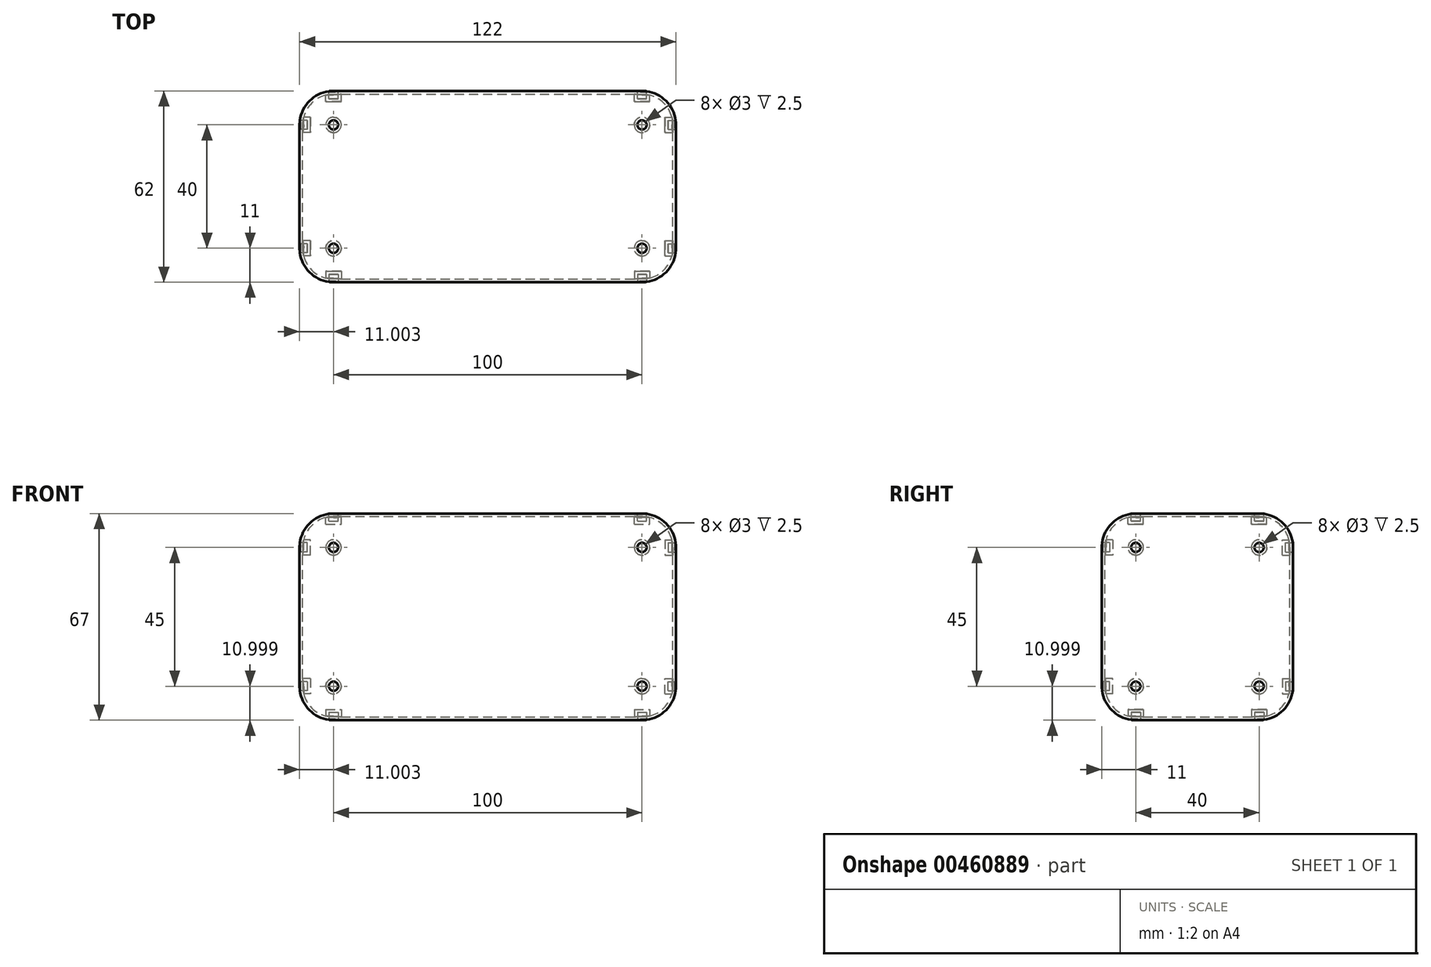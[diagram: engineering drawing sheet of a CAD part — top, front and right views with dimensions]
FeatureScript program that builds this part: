
annotation { "Feature Type Name" : "Feature", "Feature Type Description" : "" }
export const myFeature = defineFeature(function(context is Context, id is Id, definition is map)
    precondition{}
    {
        {
            var Q0;
            Q0=qCreatedBy(makeId("Front.planeOp"),FACE);
            var sketch = newSketch(context, id + "F0", { "sketchPlane" : qUnion([Q0])});
            skLineSegment(sketch, "E0.bottom", {"start": v(-60.1, -32.4) * mm, "end": v(59.9, -32.4) * mm});
            skLineSegment(sketch, "E0.top", {"start": v(-60.1, 32.6) * mm, "end": v(59.9, 32.6) * mm});
            skLineSegment(sketch, "E0.left", {"start": v(-60.1, -32.4) * mm, "end": v(-60.1, 32.6) * mm});
            skLineSegment(sketch, "E0.right", {"start": v(59.9, -32.4) * mm, "end": v(59.9, 32.6) * mm});
            skSolve(sketch);
        }
        {
            var Q0;
            Q0=makeQuery(id+"F0.imprint","IMPRINT",FACE,{"disambiguationData":[TD([[makeQuery(id+"F0.imprint","IMPRINT",EDGE,{"derivedFrom":sQuery(id+"F0.wireOp",EDGE,"E0.bottom")}),1.0]])]});
            extrude(context, id + "F1", {"entities" : qUnion([Q0]), "endBound" : BoundingType.SYMMETRIC, "depth" : 60 * mm});
        }
        {
            var Q0;
            Q0=makeQuery(id+"F1.opExtrude","CAP_EDGE",EDGE,{"disambiguationData":[OSD([sQuery(id+"F0.wireOp",EDGE,"E0.bottom")])],"isStart":false});
            var Q1;
            Q1=makeQuery(id+"F1.opExtrude","SWEPT_EDGE",EDGE,{"disambiguationData":[OSD([sQuery(id+"F0.wireOp",EDGE,"E0.bottom"),sQuery(id+"F0.wireOp",EDGE,"E0.right")])]});
            var Q2;
            Q2=makeQuery(id+"F1.opExtrude","CAP_EDGE",EDGE,{"disambiguationData":[OSD([sQuery(id+"F0.wireOp",EDGE,"E0.bottom")])],"isStart":true});
            var Q3;
            Q3=makeQuery(id+"F1.opExtrude","SWEPT_EDGE",EDGE,{"disambiguationData":[OSD([sQuery(id+"F0.wireOp",EDGE,"E0.bottom"),sQuery(id+"F0.wireOp",EDGE,"E0.left")])]});
            var Q4;
            Q4=makeQuery(id+"F1.opExtrude","CAP_EDGE",EDGE,{"disambiguationData":[OSD([sQuery(id+"F0.wireOp",EDGE,"E0.top")])],"isStart":false});
            var Q5;
            Q5=makeQuery(id+"F1.opExtrude","SWEPT_EDGE",EDGE,{"disambiguationData":[OSD([sQuery(id+"F0.wireOp",EDGE,"E0.top"),sQuery(id+"F0.wireOp",EDGE,"E0.right")])]});
            var Q6;
            Q6=makeQuery(id+"F1.opExtrude","SWEPT_EDGE",EDGE,{"disambiguationData":[OSD([sQuery(id+"F0.wireOp",EDGE,"E0.top"),sQuery(id+"F0.wireOp",EDGE,"E0.left")])]});
            var Q7;
            Q7=makeQuery(id+"F1.opExtrude","CAP_EDGE",EDGE,{"disambiguationData":[OSD([sQuery(id+"F0.wireOp",EDGE,"E0.top")])],"isStart":true});
            var Q8;
            Q8=makeQuery(id+"F1.opExtrude","CAP_EDGE",EDGE,{"disambiguationData":[OSD([sQuery(id+"F0.wireOp",EDGE,"E0.left")])],"isStart":true});
            var Q9;
            Q9=makeQuery(id+"F1.opExtrude","CAP_EDGE",EDGE,{"disambiguationData":[OSD([sQuery(id+"F0.wireOp",EDGE,"E0.left")])],"isStart":false});
            var Q10;
            Q10=makeQuery(id+"F1.opExtrude","CAP_EDGE",EDGE,{"disambiguationData":[OSD([sQuery(id+"F0.wireOp",EDGE,"E0.right")])],"isStart":false});
            var Q11;
            Q11=makeQuery(id+"F1.opExtrude","CAP_EDGE",EDGE,{"disambiguationData":[OSD([sQuery(id+"F0.wireOp",EDGE,"E0.right")])],"isStart":true});
            fillet(context, id + "F2", {"entities" : qUnion([Q0, Q1, Q2, Q3, Q4, Q5, Q6, Q7, Q8, Q9, Q10, Q11]), "radius" : 10 * mm, "tangentPropagation" : true, "allowEdgeOverflow" : false});
        }
        {
            var Q0;
            Q0=makeQuery(id+"F6BkHbIezpgDsOa_1.boolean.opBoolean","MERGE",FACE,{"derivedFrom":[makeQuery(id+"F1.opExtrude","CAP_FACE",FACE,{"disambiguationData":[OSD([sQuery(id+"F0.wireOp",EDGE,"E0.bottom"),sQuery(id+"F0.wireOp",EDGE,"E0.top"),sQuery(id+"F0.wireOp",EDGE,"E0.left"),sQuery(id+"F0.wireOp",EDGE,"E0.right")])],"isStart":false}),makeQuery(id+"F6BkHbIezpgDsOa_1.opExtrude","SWEPT_FACE",FACE,{"disambiguationData":[OSD([sQuery(id+"F58sligkbCnNzvr_1.wireOp",EDGE,"tuWzMt7B-oSg9-EDmv-xbvo-XIB2BGwvhWGn")])]})]});
            var sketch = newSketch(context, id + "F3", { "sketchPlane" : qUnion([Q0])});
            skCircle(sketch, "E1", {"center": v(-50.1, 22.6) * mm, "radius": 2.5 * mm});
            skCircle(sketch, "E2", {"center": v(49.9, 22.6) * mm, "radius": 2.5 * mm});
            skCircle(sketch, "E3", {"center": v(-50.1, -22.4) * mm, "radius": 2.5 * mm});
            skCircle(sketch, "E4", {"center": v(49.9, -22.4) * mm, "radius": 2.5 * mm});
            skSolve(sketch);
        }
        {
            var Q0;
            Q0 = qSketchRegion(id + "F3", true);
            extrude(context, id + "F4", {"entities" : qUnion([Q0]), "operationType" : NewBodyOperationType.REMOVE, "oppositeDirection" : true, "depth" : 2.5 * mm});
        }
        {
            var Q0;
            Q0=makeQuery(id+"F1.opExtrude","SWEPT_FACE",FACE,{"disambiguationData":[OSD([sQuery(id+"F0.wireOp",EDGE,"E0.right")])]});
            var sketch = newSketch(context, id + "F5", { "sketchPlane" : qUnion([Q0])});
            skCircle(sketch, "E5", {"center": v(-20, 22.6) * mm, "radius": 2.5 * mm});
            skCircle(sketch, "E6", {"center": v(20, 22.6) * mm, "radius": 2.5 * mm});
            skCircle(sketch, "E7", {"center": v(-20, -22.4) * mm, "radius": 2.5 * mm});
            skCircle(sketch, "E8", {"center": v(20, -22.4) * mm, "radius": 2.5 * mm});
            skSolve(sketch);
        }
        {
            var Q0;
            Q0 = qSketchRegion(id + "F5", true);
            extrude(context, id + "F6", {"entities" : qUnion([Q0]), "operationType" : NewBodyOperationType.REMOVE, "oppositeDirection" : true, "depth" : 2.5 * mm});
        }
        {
            var Q0;
            Q0=makeQuery(id+"F1.opExtrude","CAP_FACE",FACE,{"disambiguationData":[OSD([sQuery(id+"F0.wireOp",EDGE,"E0.bottom"),sQuery(id+"F0.wireOp",EDGE,"E0.top"),sQuery(id+"F0.wireOp",EDGE,"E0.left"),sQuery(id+"F0.wireOp",EDGE,"E0.right")])],"isStart":true});
            var sketch = newSketch(context, id + "F7", { "sketchPlane" : qUnion([Q0])});
            skCircle(sketch, "E9", {"center": v(-49.9, -22.4) * mm, "radius": 2.5 * mm});
            skCircle(sketch, "E10", {"center": v(50.1, -22.4) * mm, "radius": 2.5 * mm});
            skCircle(sketch, "E11", {"center": v(50.1, 22.6) * mm, "radius": 2.5 * mm});
            skCircle(sketch, "E12", {"center": v(-49.9, 22.6) * mm, "radius": 2.5 * mm});
            skSolve(sketch);
        }
        {
            var Q0;
            Q0 = qSketchRegion(id + "F7", true);
            extrude(context, id + "F8", {"entities" : qUnion([Q0]), "operationType" : NewBodyOperationType.REMOVE, "oppositeDirection" : true, "depth" : 2.5 * mm});
        }
        {
            var Q0;
            Q0=makeQuery(id+"F1.opExtrude","SWEPT_FACE",FACE,{"disambiguationData":[OSD([sQuery(id+"F0.wireOp",EDGE,"E0.left")])]});
            var sketch = newSketch(context, id + "F9", { "sketchPlane" : qUnion([Q0])});
            skCircle(sketch, "E13", {"center": v(-20, 22.6) * mm, "radius": 2.5 * mm});
            skCircle(sketch, "E14", {"center": v(20, 22.6) * mm, "radius": 2.5 * mm});
            skCircle(sketch, "E15", {"center": v(-20, -22.4) * mm, "radius": 2.5 * mm});
            skCircle(sketch, "E16", {"center": v(20, -22.4) * mm, "radius": 2.5 * mm});
            skSolve(sketch);
        }
        {
            var Q0;
            Q0 = qSketchRegion(id + "F9", true);
            extrude(context, id + "F10", {"entities" : qUnion([Q0]), "operationType" : NewBodyOperationType.REMOVE, "oppositeDirection" : true, "depth" : 2.5 * mm});
        }
        {
            var Q0;
            Q0=makeQuery(id+"F1.opExtrude","SWEPT_FACE",FACE,{"disambiguationData":[OSD([sQuery(id+"F0.wireOp",EDGE,"E0.bottom")])]});
            var sketch = newSketch(context, id + "F11", { "sketchPlane" : qUnion([Q0])});
            skCircle(sketch, "E17", {"center": v(-50.1, 20) * mm, "radius": 2.5 * mm});
            skCircle(sketch, "E18", {"center": v(-50.1, -20) * mm, "radius": 2.5 * mm});
            skCircle(sketch, "E19", {"center": v(49.9, -20) * mm, "radius": 2.5 * mm});
            skCircle(sketch, "E20", {"center": v(49.9, 20) * mm, "radius": 2.5 * mm});
            skSolve(sketch);
        }
        {
            var Q0;
            Q0 = qSketchRegion(id + "F11", true);
            extrude(context, id + "F12", {"entities" : qUnion([Q0]), "operationType" : NewBodyOperationType.REMOVE, "oppositeDirection" : true, "depth" : 2.5 * mm});
        }
        {
            var Q0;
            Q0=makeQuery(id+"F1.opExtrude","SWEPT_FACE",FACE,{"disambiguationData":[OSD([sQuery(id+"F0.wireOp",EDGE,"E0.top")])]});
            var sketch = newSketch(context, id + "F13", { "sketchPlane" : qUnion([Q0])});
            skCircle(sketch, "E21", {"center": v(-50.1, 20) * mm, "radius": 2.5 * mm});
            skCircle(sketch, "E22", {"center": v(-50.1, -20) * mm, "radius": 2.5 * mm});
            skCircle(sketch, "E23", {"center": v(49.9, 20) * mm, "radius": 2.5 * mm});
            skCircle(sketch, "E24", {"center": v(49.9, -20) * mm, "radius": 2.5 * mm});
            skSolve(sketch);
        }
        {
            var Q0;
            Q0 = qSketchRegion(id + "F13", true);
            extrude(context, id + "F14", {"entities" : qUnion([Q0]), "operationType" : NewBodyOperationType.REMOVE, "oppositeDirection" : true, "depth" : 2.5 * mm});
        }
        {
            var Q0;
            Q0=makeQuery(id+"F1.opExtrude","CAP_FACE",FACE,{"disambiguationData":[OSD([sQuery(id+"F0.wireOp",EDGE,"E0.bottom"),sQuery(id+"F0.wireOp",EDGE,"E0.top"),sQuery(id+"F0.wireOp",EDGE,"E0.left"),sQuery(id+"F0.wireOp",EDGE,"E0.right")])],"isStart":false});
            var sketch = newSketch(context, id + "F15", { "sketchPlane" : qUnion([Q0])});
            skPoint(sketch, "E25.oppositeSnap0", {"position": v(49.9, 0.1) * mm});
            skLineSegment(sketch, "E25.bottom", {"start": v(-77.57, 88.4) * mm, "end": v(80.68, 88.4) * mm});
            skLineSegment(sketch, "E25.top", {"start": v(-77.57, 0.1) * mm, "end": v(80.68, 0.1) * mm});
            skLineSegment(sketch, "E25.left", {"start": v(-77.57, 88.4) * mm, "end": v(-77.57, 0.1) * mm});
            skLineSegment(sketch, "E25.right", {"start": v(80.68, 88.4) * mm, "end": v(80.68, 0.1) * mm});
            skSolve(sketch);
        }
        {
            var Q0;
            Q0 = qSketchRegion(id + "F15", true);
            extrude(context, id + "F16", {"entities" : qUnion([Q0]), "operationType" : NewBodyOperationType.REMOVE, "oppositeDirection" : true, "depth" : 60 * mm});
        }
        {
            var Q0;
            Q0=makeQuery(id+"F16.boolean.opBoolean","COPY",FACE,{"derivedFrom":makeQuery(id+"F16.opExtrude","SWEPT_FACE",FACE,{"disambiguationData":[OSD([sQuery(id+"F15.wireOp",EDGE,"E25.top")])]})});
            shell(context, id + "F17", {"entities" : qUnion([Q0]), "thickness" : 1 * mm, "oppositeDirection" : true});
        }
        {
            var Q0;
            Q0=makeQuery(id+"F1.opExtrude","SWEPT_BODY",BODY,{"disambiguationData":[OSD([sQuery(id+"F0.wireOp",EDGE,"E0.bottom"),sQuery(id+"F0.wireOp",EDGE,"E0.top"),sQuery(id+"F0.wireOp",EDGE,"E0.left"),sQuery(id+"F0.wireOp",EDGE,"E0.right")])]});
            var Q1;
            Q1=makeQuery(id+"F16.boolean.opBoolean","COPY",FACE,{"derivedFrom":makeQuery(id+"F16.opExtrude","SWEPT_FACE",FACE,{"disambiguationData":[OSD([sQuery(id+"F15.wireOp",EDGE,"E25.top")])]})});
            mirror(context, id + "F18", {"operationType" : NewBodyOperationType.ADD, "entities" : qUnion([Q0]), "mirrorPlane" : qUnion([Q1])});
        }
    });
